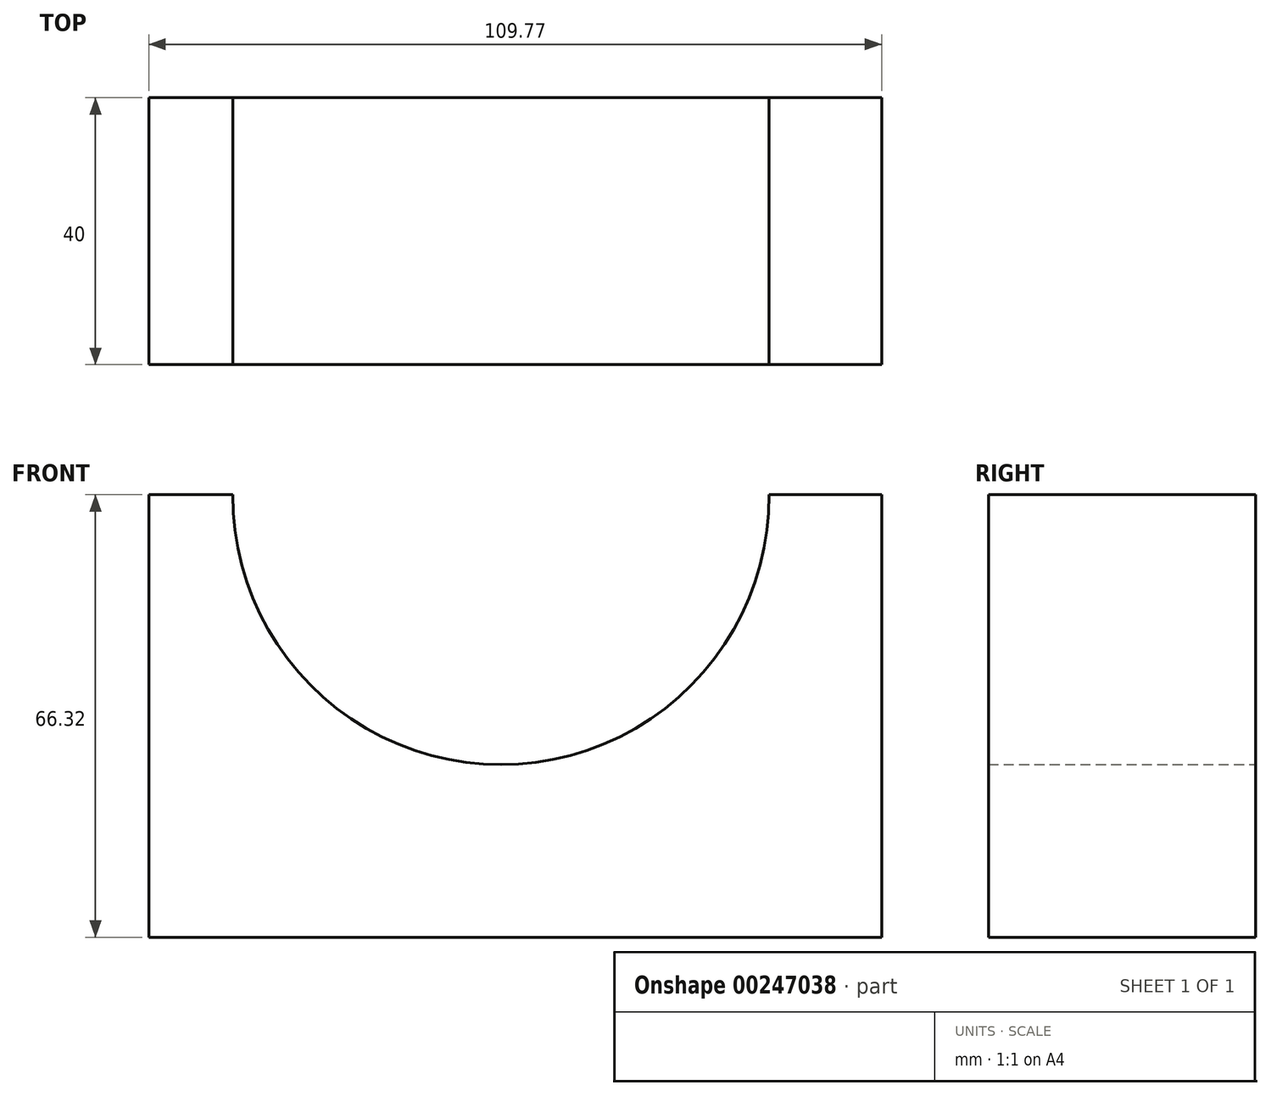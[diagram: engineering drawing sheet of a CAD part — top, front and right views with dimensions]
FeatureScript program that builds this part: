
annotation { "Feature Type Name" : "Feature", "Feature Type Description" : "" }
export const myFeature = defineFeature(function(context is Context, id is Id, definition is map)
    precondition{}
    {
        {
            var Q0;
            Q0=qCreatedBy(makeId("Front.planeOp"),FACE);
            var sketch = newSketch(context, id + "F0", { "sketchPlane" : qUnion([Q0])});
            skLineSegment(sketch, "E0", {"start": v(-52.17, 40.45) * mm, "end": v(-52.17, -25.87) * mm});
            skLineSegment(sketch, "E1", {"start": v(-52.17, -25.87) * mm, "end": v(57.6, -25.87) * mm});
            skLineSegment(sketch, "E2", {"start": v(57.6, -25.87) * mm, "end": v(57.6, 40.45) * mm});
            skLineSegment(sketch, "E3", {"start": v(57.6, 40.45) * mm, "end": v(40.73, 40.45) * mm});
            skArc(sketch, "E4", {"start": v(-39.59, 40.45) * mm, "mid": v(0.57, 0) * mm, "end": v(40.73, 40.45) * mm});
            skLineSegment(sketch, "E5.trimOffspring", {"start": v(-39.59, 40.45) * mm, "end": v(-52.17, 40.45) * mm});
            skSolve(sketch);
        }
        {
            var Q0;
            Q0 = qSketchRegion(id + "F0", true);
            extrude(context, id + "F1", {"entities" : qUnion([Q0]), "endBound" : BoundingType.SYMMETRIC, "depth" : 40 * mm});
        }
    });
